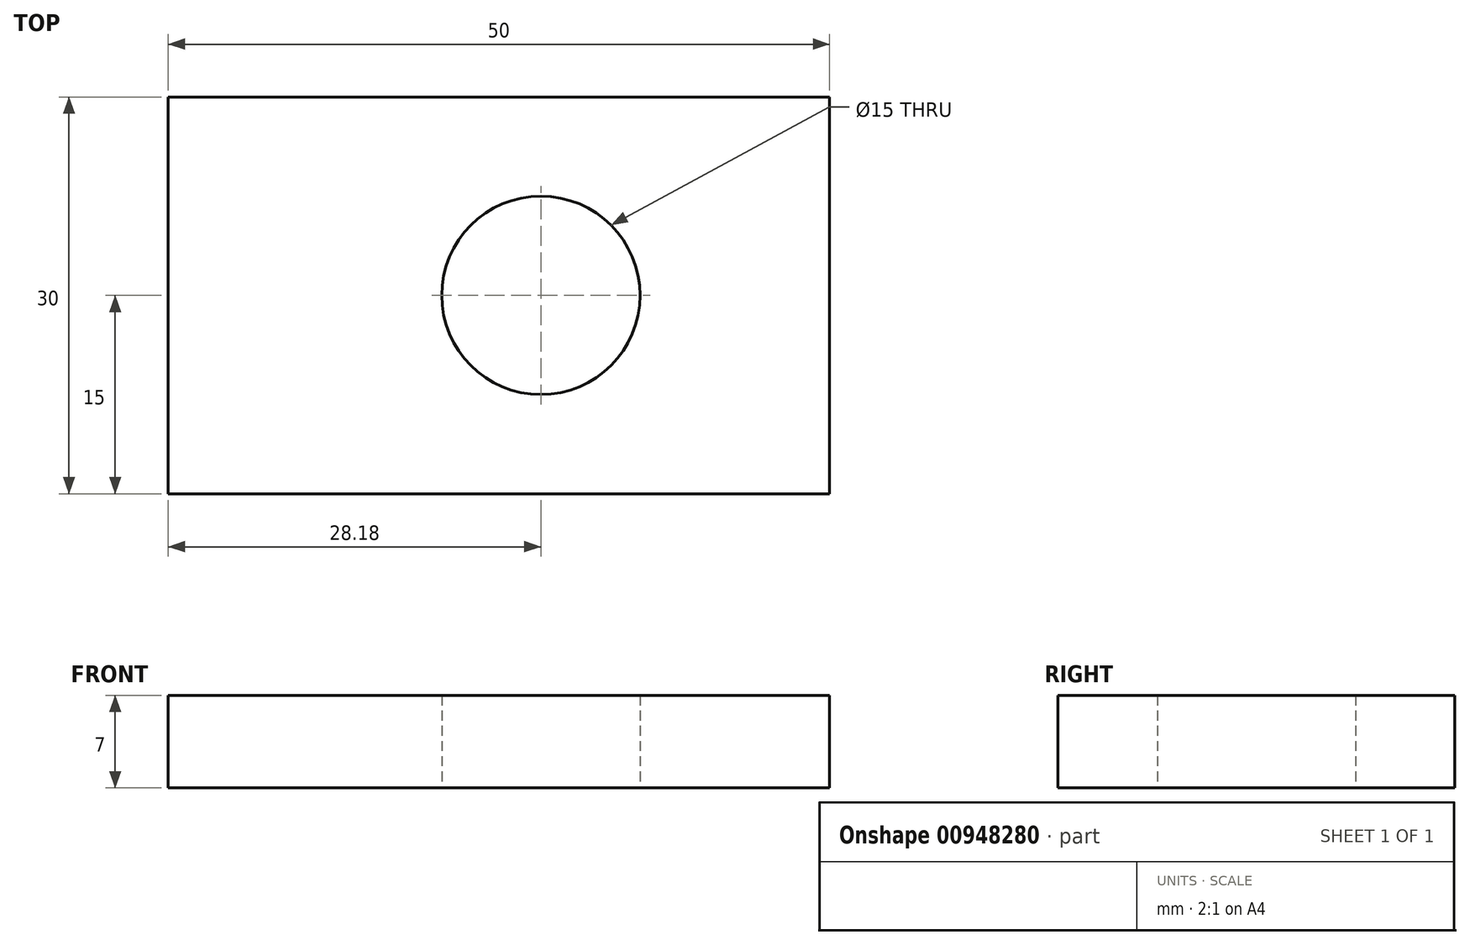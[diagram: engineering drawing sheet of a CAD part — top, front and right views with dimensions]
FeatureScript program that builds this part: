
annotation { "Feature Type Name" : "Feature", "Feature Type Description" : "" }
export const myFeature = defineFeature(function(context is Context, id is Id, definition is map)
    precondition{}
    {
        {
            var Q0;
            Q0=qCreatedBy(makeId("Top.planeOp"),FACE);
            var sketch = newSketch(context, id + "F0", { "sketchPlane" : qUnion([Q0])});
            skLineSegment(sketch, "E0.bottom", {"start": v(21.82, -15) * mm, "end": v(-28.18, -15) * mm});
            skLineSegment(sketch, "E0.top", {"start": v(21.82, 15) * mm, "end": v(-28.18, 15) * mm});
            skLineSegment(sketch, "E0.left", {"start": v(21.82, -15) * mm, "end": v(21.82, 15) * mm});
            skLineSegment(sketch, "E0.right", {"start": v(-28.18, -15) * mm, "end": v(-28.18, 15) * mm});
            skCircle(sketch, "E1", {"center": v(0, 0) * mm, "radius": 7.5 * mm});
            skSolve(sketch);
        }
        {
            var Q0;
            Q0 = qSketchRegion(id + "F0", true);
            extrude(context, id + "F1", {"entities" : qUnion([Q0]), "depth" : 7 * mm, "offsetDistance" : 25 * mm});
        }
    });
